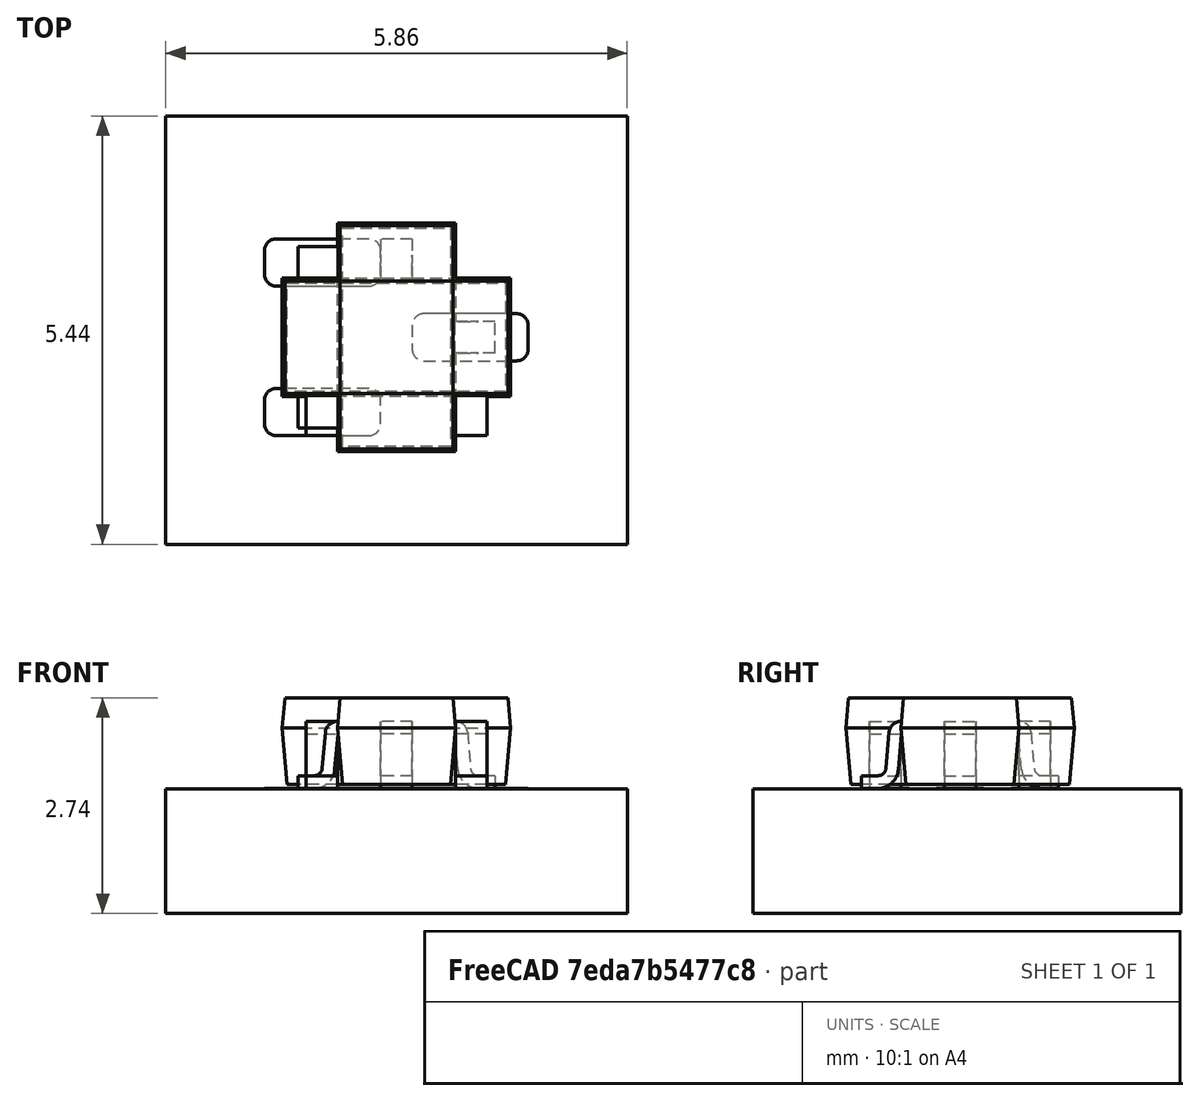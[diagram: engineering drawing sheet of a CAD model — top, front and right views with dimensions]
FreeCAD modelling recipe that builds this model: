
FCSTD DOCUMENT  (FreeCAD 1.0R39285 (Git))
Label: 2SC3325
License: All rights reserved
LicenseURL: https://en.wikipedia.org/wiki/All_rights_reserved
objects: Part::Feature×10, Sketcher::SketchObject×3, App::Part×1, Part::MultiFuse×1, App::DocumentObjectGroup×1
note: 17 computed .brp shape members not serialized (recipe doc carries the construction recipe); baked Part::Feature solids carry a one-line shape summary decoded from their .brp

FEATURE [Part::Feature] Part__Feature  label="S-Mini"
  shape: bbox 2.9 x 1.5 x 1.1 mm, 10 faces (baked)
FEATURE [Part::Feature] Part__Feature001  label="S-Mini001"
  shape: bbox 0.4 x 0.507 x 0.85 mm, 13 faces (baked)
FEATURE [Part::Feature] Part__Feature002  label="S-Mini002"
  shape: bbox 0.4 x 0.507 x 0.85 mm, 13 faces (baked)
FEATURE [Part::Feature] Part__Feature003  label="S-Mini003"
  shape: bbox 0.4 x 0.507 x 0.85 mm, 13 faces (baked)
FEATURE [App::Part] S_Mini  label="S-Mini004"
  Group = -> [Part__Feature,Part__Feature001,Part__Feature002,Part__Feature003]
  Origin = -> Origin
FEATURE [Part::MultiFuse] Fusion
  Shapes = -> [Part__Feature003,Part__Feature002,Part__Feature001,Part__Feature]
FEATURE [Part::Feature] Shape001  label="topPads"
  Placement = pos=(0,0,-0.01) rot=(0,0,1;0rad)
  shape: bbox 3.35 x 2.5 x 0.01 mm, 30 faces, 3 solids (baked)
FEATURE [Part::Feature] Shape  label="F.SilkS_outline_"
  Placement = pos=(0,0,0.01) rot=(0,0,1;0rad)
  shape: bbox 2.173 x 3.52 x 2e-07 mm, 0 faces, 0 solids (baked)
FEATURE [Sketcher::SketchObject] _F_SilkS__sketch  label="F.SilkS_"
  ArcFitTolerance = 1e-06
  FullyConstrained = false
  MakeInternals = false
  Placement = pos=(0,0,0.01) rot=(0,0,1;0rad)
  sketch-geometry (7):
    g0: LineSegment StartX=0 StartY=1.56 StartZ=0 EndX=-0.65 EndY=1.56 EndZ=0
    g1: LineSegment StartX=0 StartY=1.56 StartZ=0 EndX=0.65 EndY=1.56 EndZ=0
    g2: LineSegment StartX=0 StartY=-1.56 StartZ=0 EndX=-0.65 EndY=-1.56 EndZ=0
    g3: LineSegment StartX=0 StartY=-1.56 StartZ=0 EndX=0.65 EndY=-1.56 EndZ=0
    g4: LineSegment StartX=-1.1625 StartY=1.51 StartZ=0 EndX=-0.9225 EndY=1.84 EndZ=0
    g5: LineSegment StartX=-0.9225 StartY=1.84 StartZ=0 EndX=-1.4025 EndY=1.84 EndZ=0
    g6: LineSegment StartX=-1.4025 StartY=1.84 StartZ=0 EndX=-1.1625 EndY=1.51 EndZ=0
  constraints (3):
    c: Coincident(g4,g5)
    c: Coincident(g5,g6)
    c: Coincident(g6,g4)
FEATURE [Part::Feature] Shape002  label="F.CrtYd_outline_"
  Placement = pos=(0,0,0.01) rot=(0,0,1;0rad)
  shape: bbox 3.91 x 3.45 x 2e-07 mm, 0 faces, 0 solids (baked)
FEATURE [Sketcher::SketchObject] _F_CrtYd__sketch  label="F.CrtYd_"
  ArcFitTolerance = 1e-06
  FullyConstrained = false
  MakeInternals = false
  Placement = pos=(0,0,0.01) rot=(0,0,1;0rad)
  sketch-geometry (12):
    g0: LineSegment StartX=-1.93 StartY=1.5 StartZ=0 EndX=-0.9 EndY=1.5 EndZ=0
    g1: LineSegment StartX=-1.93 StartY=-1.5 StartZ=0 EndX=-1.93 EndY=1.5 EndZ=0
    g2: LineSegment StartX=-0.9 StartY=1.7 StartZ=0 EndX=0.9 EndY=1.7 EndZ=0
    g3: LineSegment StartX=-0.9 StartY=1.5 StartZ=0 EndX=-0.9 EndY=1.7 EndZ=0
    g4: LineSegment StartX=-0.9 StartY=-1.5 StartZ=0 EndX=-1.93 EndY=-1.5 EndZ=0
    g5: LineSegment StartX=-0.9 StartY=-1.7 StartZ=0 EndX=-0.9 EndY=-1.5 EndZ=0
    g6: LineSegment StartX=0.9 StartY=1.7 StartZ=0 EndX=0.9 EndY=0.55 EndZ=0
    g7: LineSegment StartX=0.9 StartY=0.55 StartZ=0 EndX=1.93 EndY=0.55 EndZ=0
    g8: LineSegment StartX=0.9 StartY=-0.55 StartZ=0 EndX=0.9 EndY=-1.7 EndZ=0
    g9: LineSegment StartX=0.9 StartY=-1.7 StartZ=0 EndX=-0.9 EndY=-1.7 EndZ=0
    g10: LineSegment StartX=1.93 StartY=0.55 StartZ=0 EndX=1.93 EndY=-0.55 EndZ=0
    g11: LineSegment StartX=1.93 StartY=-0.55 StartZ=0 EndX=0.9 EndY=-0.55 EndZ=0
FEATURE [Part::Feature] Shape003  label="F.Fab_outline_"
  Placement = pos=(0,0,0.01) rot=(0,0,1;0rad)
  shape: bbox 1.4 x 3 x 2e-07 mm, 0 faces, 0 solids (baked)
FEATURE [Sketcher::SketchObject] _F_Fab__sketch  label="F.Fab_"
  ArcFitTolerance = 1e-06
  FullyConstrained = false
  MakeInternals = false
  Placement = pos=(0,0,0.01) rot=(0,0,1;0rad)
  sketch-geometry (5):
    g0: LineSegment StartX=-0.65 StartY=1.125 StartZ=0 EndX=-0.325 EndY=1.45 EndZ=0
    g1: LineSegment StartX=-0.65 StartY=-1.45 StartZ=0 EndX=-0.65 EndY=1.125 EndZ=0
    g2: LineSegment StartX=-0.325 StartY=1.45 StartZ=0 EndX=0.65 EndY=1.45 EndZ=0
    g3: LineSegment StartX=0.65 StartY=1.45 StartZ=0 EndX=0.65 EndY=-1.45 EndZ=0
    g4: LineSegment StartX=0.65 StartY=-1.45 StartZ=0 EndX=-0.65 EndY=-1.45 EndZ=0
FEATURE [Part::Feature] PCB
  shape: bbox 5.865 x 5.438 x 1.58 mm, 6 faces (baked)
FEATURE [App::DocumentObjectGroup] Group  label="SOT-23-fp"
  Group = -> [Shape001,_F_SilkS__sketch,Shape,_F_CrtYd__sketch,Shape002,_F_Fab__sketch,Shape003,PCB]
FEATURE [Part::Feature] Shape014  label="2SC3325"
  shape: bbox 2.5 x 2.9 x 1.15 mm, 43 faces (baked)
